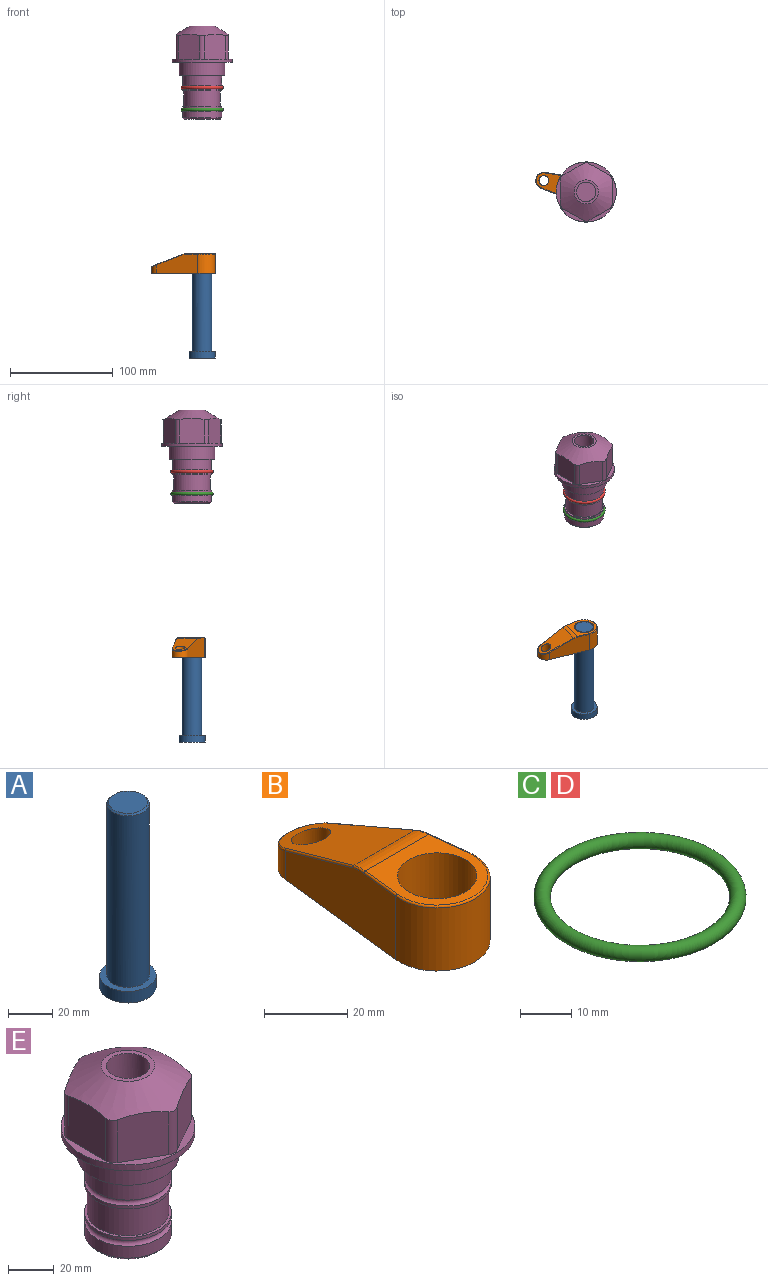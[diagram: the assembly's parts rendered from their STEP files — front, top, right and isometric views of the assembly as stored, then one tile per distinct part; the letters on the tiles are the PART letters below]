
ASSEMBLY  parts=5 mates=3
PART A: 6 faces, bbox 25.4x25.4x101.6 mm
  f0: plane 17.46x17.46mm, normal (0,0,1), area 239.5mm2, adj f5
  f1: plane 25.4x25.4mm, normal (0,0,-1), area 506.7mm2, adj f2
  f2: cylinder r=12.7mm len=25.4mm, axis (0,0,1), area 506.7mm2, adj f1,f3
  f3: plane 25.4x25.4mm, normal (0,0,1), area 221.7mm2, adj f2,f4
  f4: cylinder r=9.53mm len=94.46mm, axis (0,0,1), area 5653mm2, adj f3,f5
  f5: cone r=8.73mm half-angle=45deg, axis (0,0,-1), area 64.4mm2, adj f0,f4
PART B: 44 faces, bbox 27.5x64.5x19.1 mm
  f0: plane 2.3x0.95mm, normal (0,0,-1), area 1mm2, adj f25,f30,f34
  f1: plane 63.5x25.4mm, normal (0,0,-1), area 561.7mm2, adj f2,f3,f4,f5,f6,f7,f19,f20
  f2: cylinder r=12.7mm len=25.4mm, axis (0,0,-1), area 792.2mm2, adj f1,f3,f5,f13
  f3: plane 42.33x18.54mm, normal (0.99,0.11,0), area 647mm2, adj f1,f2,f4,f11,f12,f14
  f4: cylinder r=7.94mm len=15.78mm, axis (0,0,-1), area 158.6mm2, adj f1,f3,f5,f16
  f5: plane 42.33x18.54mm, normal (-0.99,0.11,0), area 647mm2, adj f1,f2,f4,f15,f17,f18
  f6: cylinder r=9.53mm len=19.05mm, axis (0,0,-1), area 1140.1mm2, adj f1,f8
  f7: cylinder r=4.76mm len=10.98mm, axis (0,0,-1), area 276.1mm2, adj f1,f9
  f8: plane 25.83x24.38mm, normal (0,0,1), area 262.2mm2, adj f6,f10,f11,f13,f15
  f9: plane 32.49x20.55mm, normal (0,0.34,0.94), area 489.9mm2, adj f7,f10,f14,f16,f18
  f10: cylinder r=12.7mm len=21.49mm, axis (-1,0,0), area 93.2mm2, adj f8,f9,f12,f17
  f11: cylinder r=0.51mm len=12.34mm, axis (0.11,-0.99,0), area 9.9mm2, adj f3,f8,f12,f13
  f12: bspline ~7.62x1.64mm, area 3.5mm2, adj f3,f10,f11,f14
  f13: torus R=12.19mm, axis (0,0,1), area 33.6mm2, adj f2,f8,f11,f15
  f14: cylinder r=0.51mm len=26.01mm, axis (0.1,-0.93,0.34), area 21.6mm2, adj f3,f9,f12,f16
  f15: cylinder r=0.51mm len=12.34mm, axis (0.11,0.99,0), area 9.9mm2, adj f5,f8,f13,f17
  f16: bspline ~15.78x7.05mm, area 15.7mm2, adj f4,f9,f14,f18
  f17: bspline ~7.62x1.64mm, area 3.5mm2, adj f5,f10,f15,f18
  f18: cylinder r=0.51mm len=26.01mm, axis (0.1,0.93,-0.34), area 21.6mm2, adj f5,f9,f16,f17
  f19: plane 21.6x14.29mm, normal (-0.99,-0.11,0), area 242.6mm2, adj f1,f26,f28,f34,f36,f38
  f20: plane 21.6x14.29mm, normal (0.99,-0.11,0), area 242.6mm2, adj f1,f27,f29,f37,f39,f41
  f21: cylinder r=12.7mm len=14.29mm, axis (0,0,-1), area 173.2mm2, adj f1,f26,f27,f30,f31,f33
  f22: cylinder r=7.94mm len=7.63mm, axis (0,0,-1), area 53.8mm2, adj f1,f28,f29,f42
  f23: plane 2.3x0.95mm, normal (0,0,-1), area 1mm2, adj f25,f33,f37
  f24: plane 17.94x12.32mm, normal (0,-0.34,-0.94), area 191.2mm2, adj f25,f38,f41,f42
  f25: cylinder r=9.53mm len=12.93mm, axis (-1,0,0), area 37.5mm2, adj f0,f23,f24,f31,f36,f39
  f26: cylinder r=1.59mm len=14.29mm, axis (0,0,-1), area 49mm2, adj f1,f19,f21,f32
  f27: cylinder r=1.59mm len=14.29mm, axis (0,0,-1), area 49mm2, adj f1,f20,f21,f35
  f28: cylinder r=1.59mm len=7.28mm, axis (0,0,-1), area 22.1mm2, adj f1,f19,f22,f40
  f29: cylinder r=1.59mm len=7.28mm, axis (0,0,-1), area 22.1mm2, adj f1,f20,f22,f43
  f30: torus R=14.29mm, axis (0,0,1), area 5.8mm2, adj f0,f21,f31,f32
  f31: bspline ~11.06x2.73mm, area 20.8mm2, adj f21,f25,f30,f33
  f32: sphere r=1.59mm, area 5.4mm2, adj f26,f30,f34
  f33: torus R=14.29mm, axis (0,0,1), area 5.8mm2, adj f21,f23,f31,f35
  f34: cylinder r=1.59mm len=1.68mm, axis (-0.11,0.99,0), area 2.4mm2, adj f0,f19,f32,f36
  f35: sphere r=1.59mm, area 5.4mm2, adj f27,f33,f37
  f36: bspline ~5.82x2.33mm, area 7.7mm2, adj f19,f25,f34,f38
  f37: cylinder r=1.59mm len=1.68mm, axis (0.11,0.99,0), area 2.4mm2, adj f20,f23,f35,f39
  f38: cylinder r=1.59mm len=18.33mm, axis (0.1,-0.93,0.34), area 46.7mm2, adj f19,f24,f36,f40
  f39: bspline ~5.82x2.33mm, area 7.7mm2, adj f20,f25,f37,f41
  f40: sphere r=1.59mm, area 3.6mm2, adj f28,f38,f42
  f41: cylinder r=1.59mm len=18.33mm, axis (0.1,0.93,-0.34), area 46.7mm2, adj f20,f24,f39,f43
  f42: bspline ~8.31x1.84mm, area 15.3mm2, adj f22,f24,f40,f43
  f43: sphere r=1.59mm, area 3.6mm2, adj f29,f41,f42
PART C: 1 faces, bbox 44.7x44.7x3.2 mm
  f0: torus R=19.05mm, axis (0,0,1), area 1193.9mm2
PART D: same geometry as C
PART E: 36 faces, bbox 58.7x58.7x91.2 mm
  f0: cylinder r=17.78mm len=35.56mm, axis (0,0,1), area 1670.8mm2, adj f23,f24,f31
  f1: cylinder r=19.05mm len=38.1mm, axis (0,0,1), area 1191.9mm2, adj f26,f27,f30
  f2: plane 58.66x58.66mm, normal (0,0,-1), area 1150.6mm2, adj f3,f28
  f3: cylinder r=29.33mm len=58.66mm, axis (0,0,-1), area 585.1mm2, adj f2,f4
  f4: plane 58.66x58.66mm, normal (0,0,1), area 475.9mm2, adj f3,f5,f6,f7,f8,f9,f10,f11
  f5: plane 24.5x20.32mm, normal (-0.5,0.87,0), area 562.8mm2, adj f4,f15,f16,f17
  f6: plane 24.5x20.32mm, normal (0.5,0.87,0), area 562.8mm2, adj f4,f14,f15,f17
  f7: plane 24.5x23.48mm, normal (1,0,0), area 562.8mm2, adj f4,f13,f14,f17
  f8: plane 24.5x20.32mm, normal (0.5,-0.87,0), area 562.8mm2, adj f4,f12,f13,f17
  f9: plane 24.5x20.32mm, normal (-0.5,-0.87,0), area 562.8mm2, adj f4,f11,f12,f17
  f10: plane 24.5x23.48mm, normal (-1,0,0), area 562.8mm2, adj f4,f11,f16,f17
  f11: cylinder r=5.08mm len=23.01mm, axis (0,0,-1), area 121.2mm2, adj f4,f9,f10,f17
  f12: cylinder r=5.08mm len=23.01mm, axis (0,0,-1), area 121.2mm2, adj f4,f8,f9,f17
  f13: cylinder r=5.08mm len=23.01mm, axis (0,0,-1), area 121.2mm2, adj f4,f7,f8,f17
  f14: cylinder r=5.08mm len=23.01mm, axis (0,0,-1), area 121.2mm2, adj f4,f6,f7,f17
  f15: cylinder r=5.08mm len=23.01mm, axis (0,0,-1), area 121.2mm2, adj f4,f5,f6,f17
  f16: cylinder r=5.08mm len=23.01mm, axis (0,0,-1), area 121.2mm2, adj f4,f5,f10,f17
  f17: cone r=11.73mm half-angle=60deg, axis (0,0,-1), area 2071.8mm2, adj f5,f6,f7,f8,f9,f10,f11,f12
  f18: plane 23.46x23.46mm, normal (0,0,1), area 147.4mm2, adj f17,f35
  f19: plane 34.93x34.93mm, normal (0,0,-1), area 958mm2, adj f29
  f20: cylinder r=19.05mm len=38.1mm, axis (0,0,1), area 760.1mm2, adj f21,f29
  f21: torus R=19.05mm, axis (0,0,1), area 565.3mm2, adj f20,f22
  f22: cylinder r=19.05mm len=38.1mm, axis (0,0,1), area 190mm2, adj f21,f23
  f23: plane 38.1x38.1mm, normal (0,0,1), area 146.9mm2, adj f0,f22
  f24: plane 38.1x38.1mm, normal (0,0,-1), area 146.9mm2, adj f0,f25
  f25: cylinder r=19.05mm len=38.1mm, axis (0,0,1), area 190mm2, adj f24,f26
  f26: torus R=19.05mm, axis (0,0,1), area 565.3mm2, adj f1,f25
  f27: plane 44.45x44.45mm, normal (0,0,-1), area 411.7mm2, adj f1,f28
  f28: cylinder r=22.23mm len=44.45mm, axis (0,0,1), area 1773.5mm2, adj f2,f27
  f29: cone r=19.05mm half-angle=45deg, axis (0,0,1), area 257.5mm2, adj f19,f20
  f30: cylinder r=3.17mm len=6.75mm, axis (-1,0,0), area 128mm2, adj f1,f33
  f31: cylinder r=3.17mm len=6.35mm, axis (-1,0,0), area 102.5mm2, adj f0,f33
  f32: plane 25.4x25.4mm, normal (0,0,1), area 506.7mm2, adj f33
  f33: cylinder r=12.7mm len=66.42mm, axis (0,0,-1), area 5236.2mm2, adj f30,f31,f32,f34
  f34: cone r=9.53mm half-angle=30deg, axis (0,0,-1), area 443.4mm2, adj f33,f35
  f35: cylinder r=9.53mm len=19.05mm, axis (0,0,-1), area 849mm2, adj f18,f34
PLACE A rot(axis=(0,0,1),164.4deg) t=(0,0,-260.33)mm
PLACE B rot(axis=(0,0,1),74.4deg) t=(0,0,-205.72)mm
PLACE C t=(0,0,-21.59)mm
PLACE D at identity
PLACE E at identity fixed
MATE fastened C.f0 <-> E.f0  axis (0,0,1) through (0,0,-46.1)mm
MATE cylindrical A.f2 <-> E.f0  axis (0,0,1) through (0,0,-234.7)mm
MATE fastened B.f2 <-> A.f2  axis (0,0,1) through (0,0,-186.67)mm
